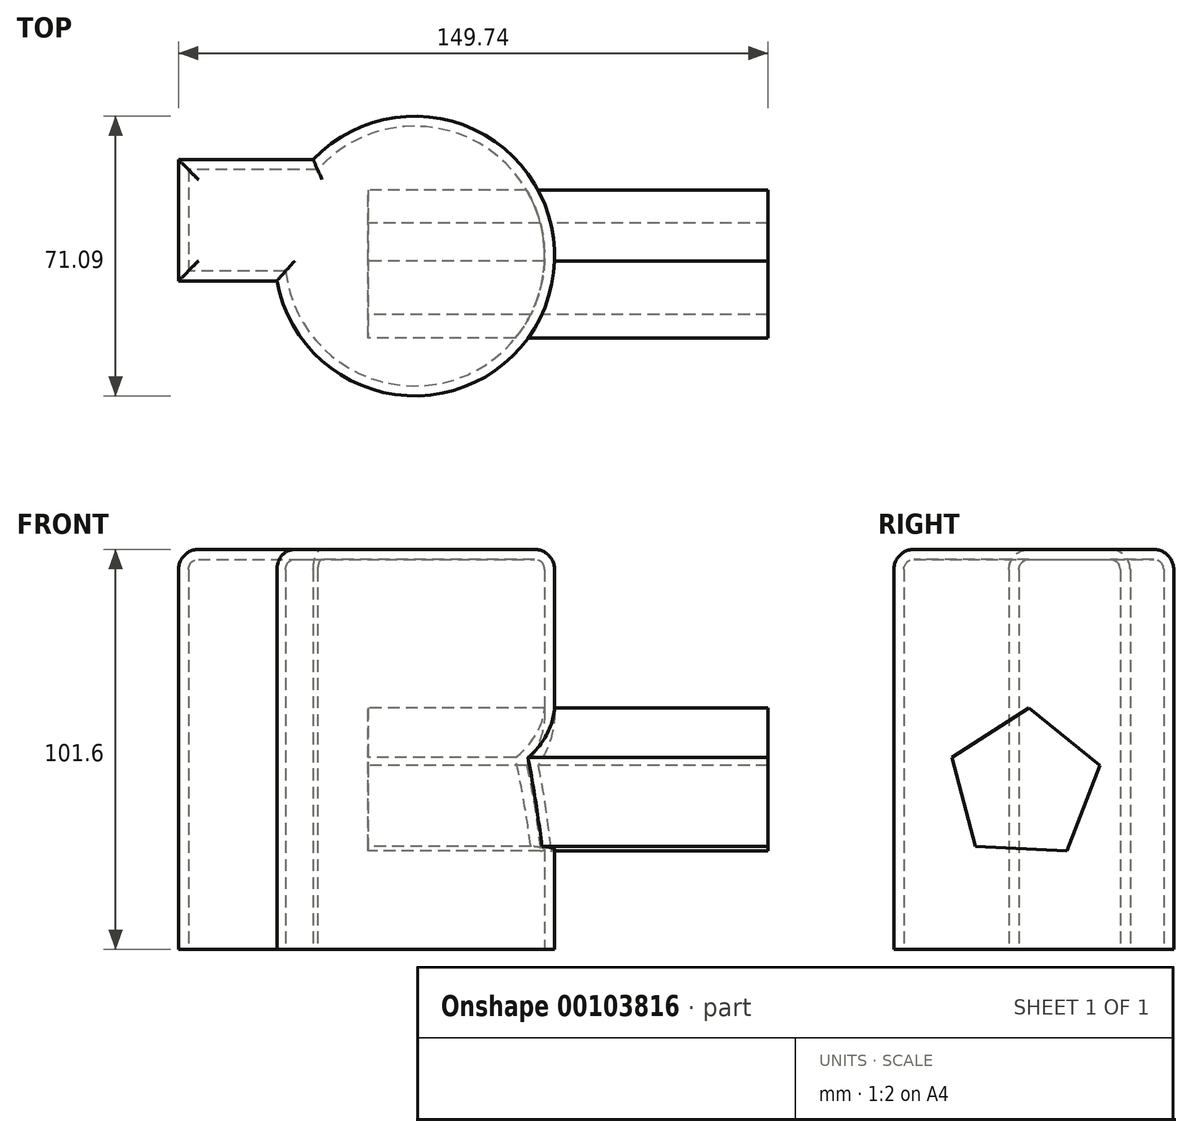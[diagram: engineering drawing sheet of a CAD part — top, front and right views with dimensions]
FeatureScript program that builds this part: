
annotation { "Feature Type Name" : "Feature", "Feature Type Description" : "" }
export const myFeature = defineFeature(function(context is Context, id is Id, definition is map)
    precondition{}
    {
        {
            var Q0;
            Q0=qCreatedBy(makeId("Top.planeOp"),FACE);
            var sketch = newSketch(context, id + "F0", { "sketchPlane" : qUnion([Q0])});
            skLineSegment(sketch, "E0.bottom", {"start": v(-13.9, 37.2) * mm, "end": v(-48.14, 37.2) * mm});
            skLineSegment(sketch, "E0.top", {"start": v(-23.12, 6.41) * mm, "end": v(-48.14, 6.41) * mm});
            skLineSegment(sketch, "E0.right", {"start": v(-48.14, 37.2) * mm, "end": v(-48.14, 6.41) * mm});
            skPoint(sketch, "E0.middle", {"position": v(-27.23, 21.8) * mm});
            skArc(sketch, "E1", {"start": v(-23.12, 6.41) * mm, "mid": v(45.92, 2.51) * mm, "end": v(-13.9, 37.2) * mm});
            skPoint(sketch, "E1.first.point", {"position": v(6.51, 47.85) * mm});
            skPoint(sketch, "E1.second.point", {"position": v(7.7, -22.6) * mm});
            skPoint(sketch, "E1.third.point", {"position": v(30.98, -17.26) * mm});
            skPoint(sketch, "E2.orphan", {"position": v(-6.31, 37.2) * mm});
            skPoint(sketch, "E3.orphan", {"position": v(-6.31, 6.41) * mm});
            skSolve(sketch);
        }
        {
            var Q0;
            Q0 = qSketchRegion(id + "F0", true);
            extrude(context, id + "F1", {"entities" : qUnion([Q0]), "depth" : 101.6 * mm});
        }
        {
            var Q0;
            Q0=makeQuery(id+"F1.opExtrude","CAP_EDGE",EDGE,{"disambiguationData":[OSD([sQuery(id+"F0.wireOp",EDGE,"E0.top")])],"isStart":false});
            var Q1;
            Q1=makeQuery(id+"F1.opExtrude","CAP_EDGE",EDGE,{"disambiguationData":[OSD([sQuery(id+"F0.wireOp",EDGE,"E1")])],"isStart":false});
            var Q2;
            Q2=makeQuery(id+"F1.opExtrude","CAP_EDGE",EDGE,{"disambiguationData":[OSD([sQuery(id+"F0.wireOp",EDGE,"E0.bottom")])],"isStart":false});
            var Q3;
            Q3=makeQuery(id+"F1.opExtrude","CAP_EDGE",EDGE,{"disambiguationData":[OSD([sQuery(id+"F0.wireOp",EDGE,"E0.right")])],"isStart":false});
            fillet(context, id + "F2", {"entities" : qUnion([Q0, Q1, Q2, Q3]), "radius" : 5.08 * mm, "tangentPropagation" : true, "allowEdgeOverflow" : false});
        }
        {
            var Q0;
            Q0=makeQuery(id+"F1.opExtrude","CAP_FACE",FACE,{"disambiguationData":[OSD([sQuery(id+"F0.wireOp",EDGE,"E0.bottom"),sQuery(id+"F0.wireOp",EDGE,"E0.top"),sQuery(id+"F0.wireOp",EDGE,"E0.right"),sQuery(id+"F0.wireOp",EDGE,"E1")])],"isStart":true});
            shell(context, id + "F3", {"entities" : qUnion([Q0]), "thickness" : 2.54 * mm});
        }
        {
            var Q0;
            Q0=qCreatedBy(makeId("Right.planeOp"),FACE);
            var sketch = newSketch(context, id + "F4", { "sketchPlane" : qUnion([Q0])});
            skCircle(sketch, "E4.cCircle", {"center": v(10.36, 41.59) * mm, "radius": 16.03 * mm, "construction": true});
            skLineSegment(sketch, "E4.0", {"start": v(29.5, 46.7) * mm, "end": v(21.14, 24.96) * mm});
            skLineSegment(sketch, "E4.1", {"start": v(21.14, 24.96) * mm, "end": v(-2.12, 26.2) * mm});
            skLineSegment(sketch, "E4.2", {"start": v(-2.12, 26.2) * mm, "end": v(-8.14, 48.7) * mm});
            skLineSegment(sketch, "E4.3", {"start": v(-8.14, 48.7) * mm, "end": v(11.4, 61.38) * mm});
            skLineSegment(sketch, "E4.4", {"start": v(11.4, 61.38) * mm, "end": v(29.5, 46.7) * mm});
            skPoint(sketch, "E4.0.midPoint", {"position": v(25.32, 35.83) * mm});
            skSolve(sketch);
        }
        {
            var Q0;
            Q0 = qSketchRegion(id + "F4", true);
            extrude(context, id + "F5", {"entities" : qUnion([Q0]), "operationType" : NewBodyOperationType.ADD, "depth" : 101.6 * mm});
        }
    });
